MODEL slx_d560c5bc5f0f
KIND model
CONFIG AbsTol = auto
CONFIG EnableMultiTasking = on
CONFIG FixedStep = auto
CONFIG MaxStep = auto
CONFIG MinStep = auto
CONFIG RelTol = 1e-3
CONFIG SampleTimeConstraint = Unconstrained
CONFIG SolverName = ode45
CONFIG StartTime = 0.0
CONFIG StopTime = 2
BLOCK [Clock] Clock
BLOCK [Scope] Controller Schedule
  Floating = off
  NumInputPorts = 1
  Ports = [1]
  ScopeSpecificationString = Simulink.scopes.TimeScopeBlockCfg('CurrentConfiguration', extmgr.ConfigurationSet(extmgr.Configuration('Core','General UI',true,'FigureColor',[0.156862745098039 0.156862745098039 0.156862745098039]),extmgr.Configuration('Core','Source UI',true),extmgr.Configuration('Sources','WiredSimulink',true,'DataLoggingVariableName','nschedule','DataLoggingSaveFormat','StructureWithTime','DataLoggingDecimatio...<+2846ch>
BLOCK [TransferFcn] DC Servo
  Denominator = [1 1 0]
  Numerator = [1000]
BLOCK [Display] Display
  Decimation = 1
  Ports = [1]
BLOCK [From] From
  CloseFcn = tagdialog Close
  GotoTag = r
  TagVisibility = global
BLOCK [From] From1
  CloseFcn = tagdialog Close
  GotoTag = y
  TagVisibility = global
BLOCK [From] From2
  CloseFcn = tagdialog Close
  GotoTag = u
  TagVisibility = global
BLOCK [From] From3
  CloseFcn = tagdialog Close
  GotoTag = y
  TagVisibility = global
BLOCK [From] From4
  CloseFcn = tagdialog Close
  GotoTag = r
  TagVisibility = global
BLOCK [Goto] Goto
  GotoTag = r
  NameLocation = right
  TagVisibility = global
BLOCK [Goto] Goto1
  GotoTag = y
  NameLocation = right
  TagVisibility = global
BLOCK [Goto] Goto2
  GotoTag = u
  TagVisibility = global
BLOCK [Mux] Mux1
  DisplayOption = bar
  Inputs = 2
  Ports = [2, 1]
BLOCK [Scope] Network Schedule
  Floating = off
  NumInputPorts = 1
  Ports = [1]
  ScopeSpecificationString = Simulink.scopes.TimeScopeBlockCfg('CurrentConfiguration', extmgr.ConfigurationSet(extmgr.Configuration('Core','General UI',true,'FigureColor',[0.156862745098039 0.156862745098039 0.156862745098039]),extmgr.Configuration('Core','Source UI',true),extmgr.Configuration('Sources','WiredSimulink',true,'DataLoggingVariableName','nschedule1','DataLoggingSaveFormat','StructureWithTime','DataLoggingDecimati...<+2883ch>
BLOCK [SignalGenerator] Reference
  Ports = [0, 1]
  WaveForm = square
BLOCK [Scope] Sensor//Actuator Schedule
  Floating = off
  NumInputPorts = 1
  Ports = [1]
  ScopeSpecificationString = Simulink.scopes.TimeScopeBlockCfg('CurrentConfiguration', extmgr.ConfigurationSet(extmgr.Configuration('Core','General UI',true,'FigureColor',[0.156862745098039 0.156862745098039 0.156862745098039]),extmgr.Configuration('Core','Source UI',true),extmgr.Configuration('Sources','WiredSimulink',true,'DataLoggingVariableName','nschedule2','DataLoggingSaveFormat','StructureWithTime','DataLoggingDecimati...<+2858ch>
BLOCK [TransportDelay] Transport Delay
  DelayTime = 0.0020
  Ports = [1, 1]
BLOCK [TransportDelay] Transport Delay1
  DelayTime = 0.0071
  Ports = [1, 1]
BLOCK [Reference] TrueTime Kernel (Controller Node)  REF=truetime/TrueTime Kernel  (lib defined in slx_0362a698a4ec)
  Ports = [1, 1]
  SourceBlock = truetime/TrueTime Kernel
BLOCK [Reference] TrueTime Kernel (Interfering Node)  REF=truetime/TrueTime Kernel  (lib defined in slx_0362a698a4ec)
  Ports = [1]
  SourceBlock = truetime/TrueTime Kernel
BLOCK [Reference] TrueTime Kernel (Sensor//Actuator Node)  REF=truetime/TrueTime Kernel  (lib defined in slx_0362a698a4ec)
  Ports = [1, 2]
  SourceBlock = truetime/TrueTime Kernel
BLOCK [Reference] TrueTime Network  REF=truetime/TrueTime Network  (lib defined in slx_0362a698a4ec)
  Ports = [0, 1]
  SourceBlock = truetime/TrueTime Network
  SourceType = Real-Time Network
BLOCK [UniformRandomNumber] Uniform Random Number
  Minimum = 0
  SampleTime = 0.001
BLOCK [Scope] r
  Floating = off
  NumInputPorts = 1
  Ports = [1]
  ScopeSpecificationString = Simulink.scopes.TimeScopeBlockCfg('CurrentConfiguration', extmgr.ConfigurationSet(extmgr.Configuration('Core','General UI',true,'FigureColor',[1 1 1]),extmgr.Configuration('Core','Source UI',true),extmgr.Configuration('Sources','WiredSimulink',true,'DataLoggingVariableName','r','DataLoggingSaveFormat','Array','DataLoggingDecimation','1','DataLoggingDecimateData',true,'DataLogging',true),extmgr.Con...<+2755ch>
BLOCK [Scope] r, y; u
  Floating = off
  NumInputPorts = 2
  Ports = [2]
  ScopeSpecificationString = Simulink.scopes.TimeScopeBlockCfg('CurrentConfiguration', extmgr.ConfigurationSet(extmgr.Configuration('Core','General UI',true,'FigureColor',[1 1 1]),extmgr.Configuration('Core','Source UI',true),extmgr.Configuration('Sources','WiredSimulink',true,'DataLoggingVariableName','y','DataLoggingDecimation','1','DataLoggingDecimateData',true,'DataLoggingSaveFormat','StructureWithTime'),extmgr.Configurat...<+4757ch>
BLOCK [Scope] y1
  Floating = off
  NumInputPorts = 1
  Ports = [1]
  ScopeSpecificationString = Simulink.scopes.TimeScopeBlockCfg('CurrentConfiguration', extmgr.ConfigurationSet(extmgr.Configuration('Core','General UI',true,'FigureColor',[1 1 1]),extmgr.Configuration('Core','Source UI',true),extmgr.Configuration('Sources','WiredSimulink',true,'DataLoggingVariableName','y1','DataLoggingSaveFormat','Array','DataLoggingDecimation','1','DataLoggingDecimateData',true,'DataLogging',true),extmgr.Co...<+2783ch>
ANNOTATION (root): TrueTime 2.0 Networked Control System <copyright redacted>
LINE Clock:1 -> Display:1
LINE DC Servo:1 -> Transport Delay1:1
LINE From1:1 -> Mux1:1
LINE From2:1 -> r, y; u:2
LINE From3:1 -> y1:1
LINE From4:1 -> r:1
LINE From:1 -> Mux1:2
LINE Mux1:1 -> r, y; u:1
NET Reference:1 -> Goto:1, TrueTime Kernel (Controller Node):1
NET Transport Delay1:1 -> Goto1:1, TrueTime Kernel (Sensor//Actuator Node):1
LINE Transport Delay:1 -> DC Servo:1
LINE TrueTime Kernel (Controller Node):1 -> Controller Schedule:1
NET TrueTime Kernel (Sensor//Actuator Node):1 -> Goto2:1, Transport Delay:1
LINE TrueTime Kernel (Sensor//Actuator Node):2 -> Sensor//Actuator Schedule:1
LINE TrueTime Network:1 -> Network Schedule:1
LINE Uniform Random Number:1 -> TrueTime Kernel (Interfering Node):1
note: NET lines group one-source signal fan-out (src -> all destinations, sorted); 1:1 wires keep LINE
